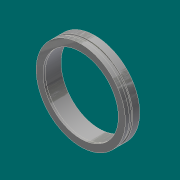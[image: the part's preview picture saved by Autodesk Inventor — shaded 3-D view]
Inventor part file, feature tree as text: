
AUTODESK INVENTOR PART (.ipt)
format: ipt  version: 2017.3 (Build 213257000, 257)  size: 211,968 bytes
history: native  units: in
note: dims shown in document units (in); Inventor stores cm internally (conversion verified against a paired STEP export)
features: revolve x1, chamfer x1, sketch x1
ambient origin geometry x8: Origin, YZ Plane, XZ Plane, XY Plane, X Axis, Y Axis, Z Axis, Center Point
bodies: Solid1 (feature_tree)
feature tree (3):
  revolve  "Revolution1"  [1 undecoded]
  chamfer  "Chamfer2"  Angle=90.0deg  [1 undecoded]
  sketch  "Sketch1"  dims[d0=16.25in d5=1.0in d6=90.0deg d13=18.75in d14=19.25in d16=1.75in d17=1.35in d18=0.0515in d19=0.0842in d20=0.0312in d21=0.125in d22=45.0deg d32=17.0in d33=0.4375in d35=0.0625in d36=0.125in d38=8.0in d43=6.1875in d44=0.5in d45=90.0deg d46=0.2577in]
note: 2 required parameter values undecoded (feature->parameter linkage not recoverable at this tier; creation-order binding heuristic only, values carry confidence <= 0.55)